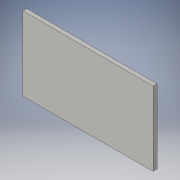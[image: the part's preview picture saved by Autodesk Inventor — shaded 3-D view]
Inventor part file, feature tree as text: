
AUTODESK INVENTOR PART (.ipt)
format: ipt  version: 2016 (Build 200138000, 138)  size: 89,088 bytes
history: native  units: in
note: dims shown in document units (in); Inventor stores cm internally (conversion verified against a paired STEP export)
features: extrude x1, sketch x1
ambient origin geometry x8: Origin, YZ Plane, XZ Plane, XY Plane, X Axis, Y Axis, Z Axis, Center Point
bodies: Solid1 (feature_tree)
feature tree (2):
  extrude  "Extrusion1"  Depth=9.375in
  sketch  "Sketch1"  dims[d0=16.5in d1=9.375in d2=0.5in d3=0.0in]
